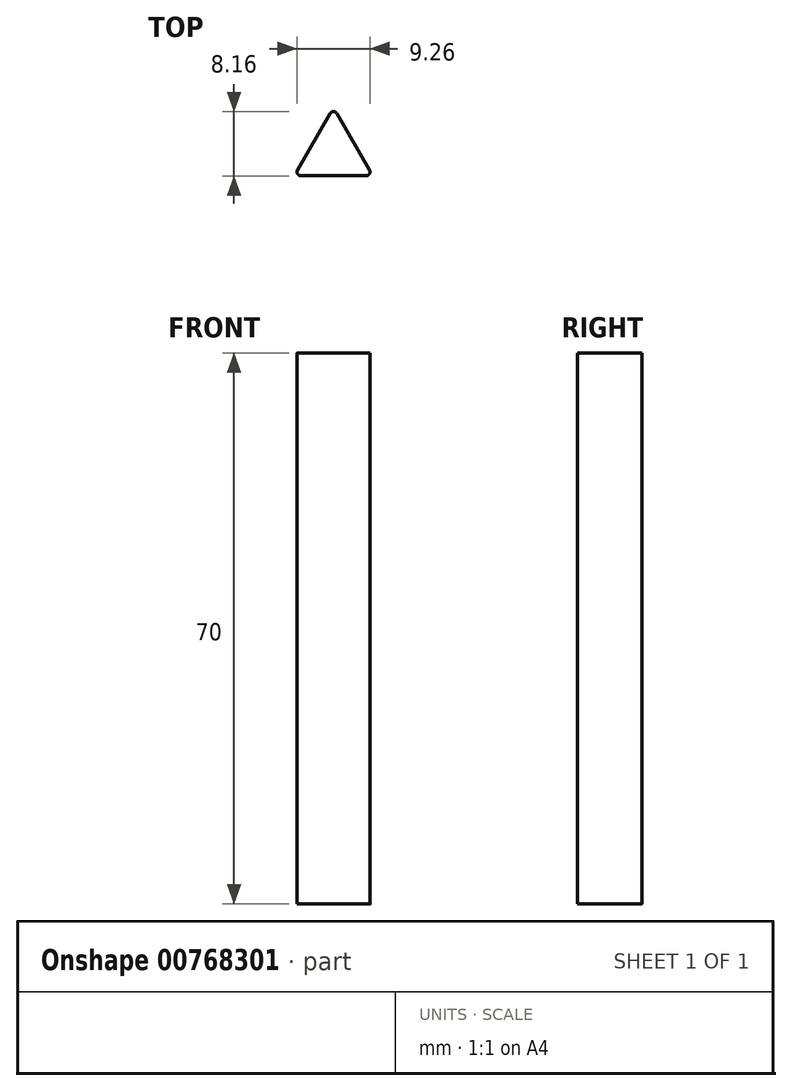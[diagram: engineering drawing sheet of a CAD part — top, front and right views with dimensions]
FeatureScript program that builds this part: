
annotation { "Feature Type Name" : "Feature", "Feature Type Description" : "" }
export const myFeature = defineFeature(function(context is Context, id is Id, definition is map)
    precondition{}
    {
        {
            var Q0;
            Q0=qCreatedBy(makeId("Top.planeOp"),FACE);
            var sketch = newSketch(context, id + "F0", { "sketchPlane" : qUnion([Q0])});
            skCircle(sketch, "E0.cCircle", {"center": v(0, 0) * mm, "radius": 5.77 * mm, "construction": true});
            skLineSegment(sketch, "E0.0", {"start": v(0.43, 5.02) * mm, "end": v(4.57, -2.14) * mm});
            skLineSegment(sketch, "E0.1", {"start": v(4.13, -2.89) * mm, "end": v(-4.13, -2.89) * mm});
            skLineSegment(sketch, "E0.2", {"start": v(-4.57, -2.14) * mm, "end": v(-0.43, 5.02) * mm});
            skPoint(sketch, "E1.visualSharp", {"position": v(0, 5.77) * mm});
            skArc(sketch, "E1.filletArc", {"start": v(0.43, 5.02) * mm, "mid": v(0, 5.27) * mm, "end": v(-0.43, 5.02) * mm});
            skPoint(sketch, "E2.visualSharp", {"position": v(5, -2.89) * mm});
            skArc(sketch, "E2.filletArc", {"start": v(4.13, -2.89) * mm, "mid": v(4.57, -2.64) * mm, "end": v(4.57, -2.14) * mm});
            skPoint(sketch, "E3.visualSharp", {"position": v(-5, -2.89) * mm});
            skArc(sketch, "E3.filletArc", {"start": v(-4.57, -2.14) * mm, "mid": v(-4.57, -2.64) * mm, "end": v(-4.13, -2.89) * mm});
            skSolve(sketch);
        }
        {
            var Q0;
            Q0=makeQuery(id+"F0.imprint","IMPRINT",FACE,{"disambiguationData":[TD([[makeQuery(id+"F0.imprint","IMPRINT",EDGE,{"derivedFrom":sQuery(id+"F0.wireOp",EDGE,"E0.0")}),-1.0]])]});
            extrude(context, id + "F1", {"entities" : qUnion([Q0]), "depth" : 70 * mm, "offsetDistance" : 25 * mm});
        }
    });
